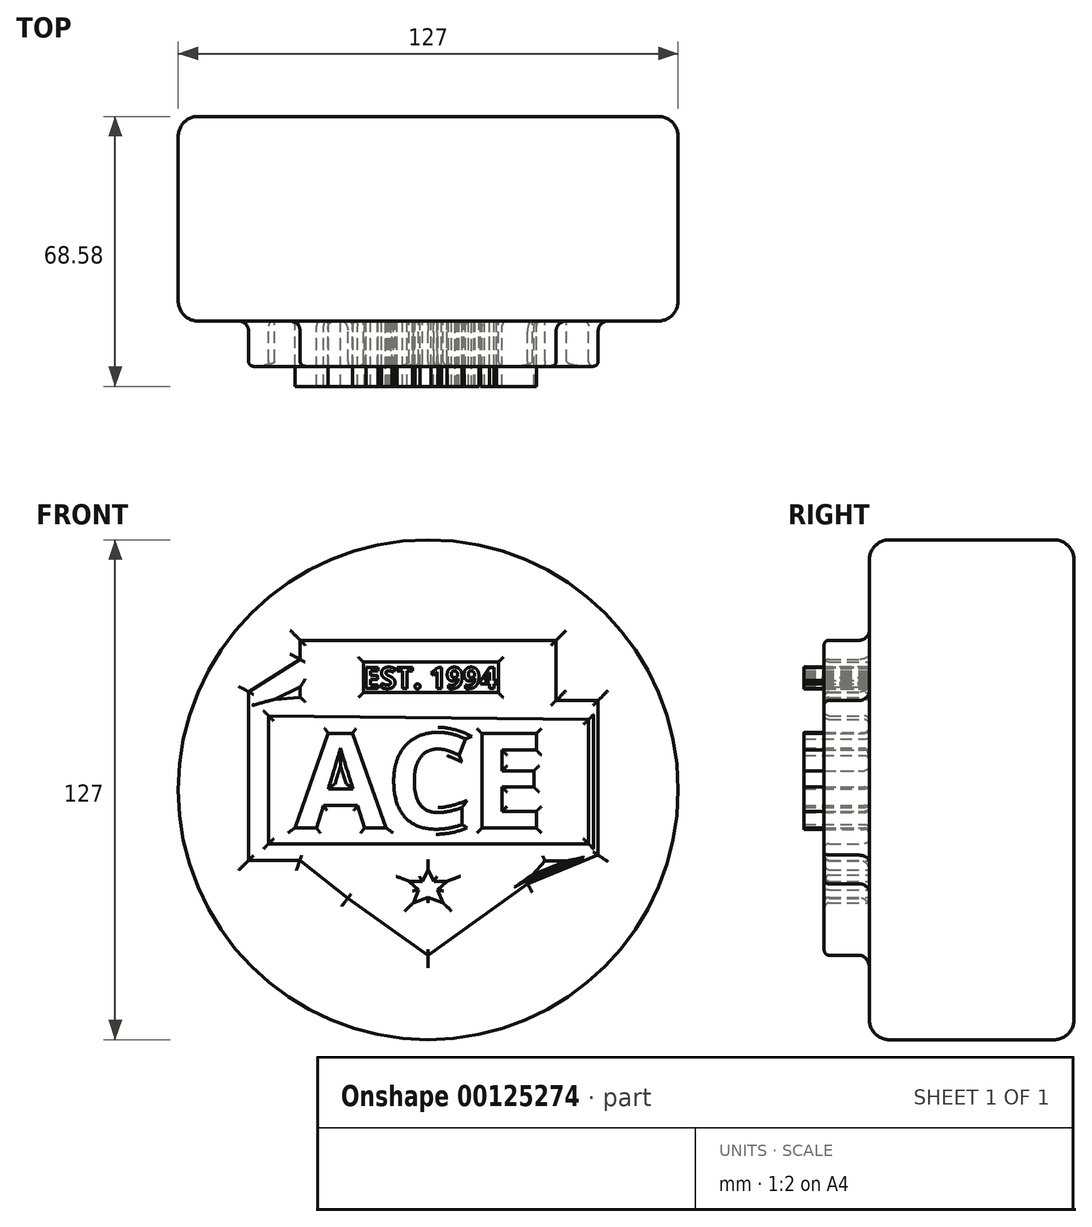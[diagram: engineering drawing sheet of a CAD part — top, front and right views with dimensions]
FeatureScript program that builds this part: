
annotation { "Feature Type Name" : "Feature", "Feature Type Description" : "" }
export const myFeature = defineFeature(function(context is Context, id is Id, definition is map)
    precondition{}
    {
        {
            var Q0;
            Q0=qCreatedBy(makeId("Front.planeOp"),FACE);
            var sketch = newSketch(context, id + "F0", { "sketchPlane" : qUnion([Q0])});
            skLineSegment(sketch, "E0", {"start": v(-32.51, 28.27) * mm, "end": v(-32.51, 37.97) * mm});
            skLineSegment(sketch, "E1", {"start": v(-32.51, 37.97) * mm, "end": v(32.51, 37.97) * mm});
            skLineSegment(sketch, "E2", {"start": v(32.51, 37.97) * mm, "end": v(32.51, 22.69) * mm});
            skLineSegment(sketch, "E3", {"start": v(32.51, 22.69) * mm, "end": v(43.19, 22.69) * mm});
            skLineSegment(sketch, "E4", {"start": v(43.19, 22.69) * mm, "end": v(43.19, -16.62) * mm});
            skLineSegment(sketch, "E5", {"start": v(43.19, -16.62) * mm, "end": v(25.23, -23.9) * mm});
            skLineSegment(sketch, "E6", {"start": v(25.23, -23.9) * mm, "end": v(0, -42.08) * mm});
            skLineSegment(sketch, "E7", {"start": v(0, -42.08) * mm, "end": v(-20.4, -27.54) * mm});
            skLineSegment(sketch, "E8", {"start": v(-20.4, -27.54) * mm, "end": v(-32.58, -17.93) * mm});
            skLineSegment(sketch, "E9", {"start": v(-32.58, -17.93) * mm, "end": v(-45.61, -17.93) * mm});
            skLineSegment(sketch, "E10", {"start": v(-45.61, -17.93) * mm, "end": v(-45.61, 21.23) * mm});
            skLineSegment(sketch, "E11", {"start": v(-45.61, 21.23) * mm, "end": v(-33.73, 21.23) * mm});
            skLineSegment(sketch, "E12", {"start": v(-32.51, 28.27) * mm, "end": v(-32.51, 21.23) * mm});
            skLineSegment(sketch, "E13", {"start": v(-45.61, 21.23) * mm, "end": v(-32.51, 28.27) * mm});
            skLineSegment(sketch, "E14", {"start": v(-45.61, 24.87) * mm, "end": v(-32.51, 33.12) * mm});
            skLineSegment(sketch, "E15", {"start": v(-32.51, 33.12) * mm, "end": v(-45.61, 24.87) * mm});
            skLineSegment(sketch, "E16", {"start": v(-45.61, 21.23) * mm, "end": v(-45.61, 24.87) * mm});
            skLineSegment(sketch, "E17", {"start": v(-40.55, 18.8) * mm, "end": v(-40.55, -13.7) * mm});
            skLineSegment(sketch, "E18", {"start": v(-40.55, -13.7) * mm, "end": v(40.73, -13.7) * mm});
            skLineSegment(sketch, "E19", {"start": v(40.73, -13.7) * mm, "end": v(40.73, 17.82) * mm});
            skLineSegment(sketch, "E20", {"start": v(40.73, 17.82) * mm, "end": v(-40.55, 18.8) * mm});
            skText(sketch, "E21", { "text": "ACE", "fontName": "OpenSans-Bold.ttf"});
            skText(sketch, "E22", { "text": "EST. 1994", "fontName": "OpenSans-Bold.ttf"});
            skLineSegment(sketch, "E23", {"start": v(26.46, -21.62) * mm, "end": v(35.2, -18.08) * mm});
            skLineSegment(sketch, "E24", {"start": v(35.2, -18.08) * mm, "end": v(29.69, -18.08) * mm});
            skLineSegment(sketch, "E25", {"start": v(29.69, -18.08) * mm, "end": v(26.46, -21.62) * mm});
            skLineSegment(sketch, "E26", {"start": v(0, -20.42) * mm, "end": v(-1.49, -23.24) * mm});
            skLineSegment(sketch, "E27", {"start": v(-1.49, -23.24) * mm, "end": v(-4.85, -23.24) * mm});
            skLineSegment(sketch, "E28", {"start": v(-4.85, -23.24) * mm, "end": v(-2.43, -25.39) * mm});
            skLineSegment(sketch, "E29", {"start": v(-2.43, -25.39) * mm, "end": v(-3.77, -28.75) * mm});
            skLineSegment(sketch, "E30", {"start": v(-3.77, -28.75) * mm, "end": v(0, -27.4) * mm});
            skLineSegment(sketch, "E31", {"start": v(0, -20.42) * mm, "end": v(0, -27.4) * mm});
            skLineSegment(sketch, "E32.MirrorCS", {"start": v(2.43, -25.39) * mm, "end": v(3.77, -28.75) * mm});
            skLineSegment(sketch, "E33.MirrorCS", {"start": v(3.77, -28.75) * mm, "end": v(0, -27.4) * mm});
            skLineSegment(sketch, "E34.MirrorCS", {"start": v(4.85, -23.24) * mm, "end": v(2.43, -25.39) * mm});
            skLineSegment(sketch, "E35.MirrorCS", {"start": v(1.49, -23.24) * mm, "end": v(4.85, -23.24) * mm});
            skLineSegment(sketch, "E36.MirrorCS", {"start": v(0, -20.42) * mm, "end": v(1.49, -23.24) * mm});
            skLineSegment(sketch, "E37", {"start": v(-32.51, 21.23) * mm, "end": v(-33.73, 21.23) * mm});
            skLineSegment(sketch, "E38", {"start": v(-38.98, 22.99) * mm, "end": v(-32.51, 26.1) * mm});
            skLineSegment(sketch, "E39", {"start": v(-32.51, 26.1) * mm, "end": v(-32.51, 23.5) * mm});
            skLineSegment(sketch, "E40", {"start": v(-32.51, 23.5) * mm, "end": v(-38.98, 22.99) * mm});
            skLineSegment(sketch, "E41.bottom", {"start": v(-16.45, 32.41) * mm, "end": v(17.83, 32.41) * mm});
            skLineSegment(sketch, "E41.top", {"start": v(-16.45, 24.65) * mm, "end": v(17.83, 24.65) * mm});
            skLineSegment(sketch, "E41.left", {"start": v(-16.45, 32.41) * mm, "end": v(-16.45, 24.65) * mm});
            skLineSegment(sketch, "E41.right", {"start": v(17.83, 32.41) * mm, "end": v(17.83, 24.65) * mm});
            const initialGuessF0  = {"E21": [-0.03384, -0.0097, 1, 0, 0.02415], "E22": [-0.01645, 0.02573, 1, 0, 0.0054]};
            skSetInitialGuess(sketch, initialGuessF0);
            skSolve(sketch);
        }
        {
            var Q0;
            Q0=makeQuery(id+"F0.imprint","IMPRINT",FACE,{"disambiguationData":[TD([[makeQuery(id+"F0.imprint","IMPRINT",EDGE,{"derivedFrom":sQuery(id+"F0.wireOp",EDGE,"E22.sketch_text.stroke-0")}),-1.0]])]});
            var Q1;
            Q1=makeQuery(id+"F0.imprint","IMPRINT",FACE,{"disambiguationData":[TD([[makeQuery(id+"F0.imprint","IMPRINT",EDGE,{"derivedFrom":sQuery(id+"F0.wireOp",EDGE,"E22.sketch_text.stroke-12")}),-1.0]])]});
            var Q2;
            Q2=makeQuery(id+"F0.imprint","IMPRINT",FACE,{"disambiguationData":[TD([[makeQuery(id+"F0.imprint","IMPRINT",EDGE,{"derivedFrom":sQuery(id+"F0.wireOp",EDGE,"E22.sketch_text.stroke-40")}),-1.0]])]});
            var Q3;
            Q3=makeQuery(id+"F0.imprint","IMPRINT",FACE,{"disambiguationData":[TD([[makeQuery(id+"F0.imprint","IMPRINT",EDGE,{"derivedFrom":sQuery(id+"F0.wireOp",EDGE,"E22.sketch_text.stroke-48")}),-1.0]])]});
            var Q4;
            Q4=makeQuery(id+"F0.imprint","IMPRINT",FACE,{"disambiguationData":[TD([[makeQuery(id+"F0.imprint","IMPRINT",EDGE,{"derivedFrom":sQuery(id+"F0.wireOp",EDGE,"E22.sketch_text.stroke-56")}),-1.0]])]});
            var Q5;
            Q5=makeQuery(id+"F0.imprint","IMPRINT",FACE,{"disambiguationData":[TD([[makeQuery(id+"F0.imprint","IMPRINT",EDGE,{"derivedFrom":sQuery(id+"F0.wireOp",EDGE,"E22.sketch_text.stroke-66")}),-1.0]])]});
            var Q6;
            Q6=makeQuery(id+"F0.imprint","IMPRINT",FACE,{"disambiguationData":[TD([[makeQuery(id+"F0.imprint","IMPRINT",EDGE,{"derivedFrom":sQuery(id+"F0.wireOp",EDGE,"E22.sketch_text.stroke-92")}),-1.0]])]});
            var Q7;
            Q7=makeQuery(id+"F0.imprint","IMPRINT",FACE,{"disambiguationData":[TD([[makeQuery(id+"F0.imprint","IMPRINT",EDGE,{"derivedFrom":sQuery(id+"F0.wireOp",EDGE,"E22.sketch_text.stroke-118")}),-1.0]])]});
            var Q8;
            {var subQ5=sQuery(id+"F0.wireOp",EDGE,"E1");Q8=makeQuery(id+"F0.imprint","IMPRINT",FACE,{"disambiguationData":[TD([[makeQuery(id+"F0.imprint","IMPRINT",EDGE,{"derivedFrom":subQ5}),-1.0]])]});}
            var Q9;
            Q9=makeQuery(id+"F0.imprint","IMPRINT",FACE,{"disambiguationData":[TD([[makeQuery(id+"F0.imprint","IMPRINT",EDGE,{"derivedFrom":sQuery(id+"F0.wireOp",EDGE,"E21.sketch_text.stroke-12")}),-1.0]])]});
            var Q10;
            Q10=makeQuery(id+"F0.imprint","IMPRINT",FACE,{"disambiguationData":[TD([[makeQuery(id+"F0.imprint","IMPRINT",EDGE,{"derivedFrom":sQuery(id+"F0.wireOp",EDGE,"E21.sketch_text.stroke-0")}),-1.0]])]});
            var Q11;
            Q11=makeQuery(id+"F0.imprint","IMPRINT",FACE,{"disambiguationData":[TD([[makeQuery(id+"F0.imprint","IMPRINT",EDGE,{"derivedFrom":sQuery(id+"F0.wireOp",EDGE,"E21.sketch_text.stroke-27")}),-1.0]])]});
            var Q12;
            {var subQ0=sQuery(id+"F0.wireOp",EDGE,"E13");Q12=makeQuery(id+"F0.imprint","IMPRINT",FACE,{"disambiguationData":[TD([[makeQuery(id+"F0.imprint","IMPRINT",EDGE,{"derivedFrom":subQ0}),1.0]])]});}
            var Q13;
            Q13=makeQuery(id+"F0.imprint","IMPRINT",FACE,{"disambiguationData":[TD([[makeQuery(id+"F0.imprint","IMPRINT",EDGE,{"derivedFrom":sQuery(id+"F0.wireOp",EDGE,"E11")}),1.0]])]});
            extrude(context, id + "F1", {"entities" : qUnion([Q0, Q1, Q2, Q3, Q4, Q5, Q6, Q7, Q8, Q9, Q10, Q11, Q12, Q13]), "depth" : 38.1 * mm, "hasSecondDirection" : true, "secondDirectionOppositeDirection" : false, "secondDirectionDepth" : 8.18 * mm});
        }
        {
            var Q0;
            Q0=qCreatedBy(makeId("Front.planeOp"),FACE);
            var sketch = newSketch(context, id + "F2", { "sketchPlane" : qUnion([Q0])});
            skCircle(sketch, "E42", {"center": v(0, 0) * mm, "radius": 63.5 * mm});
            skLineSegment(sketch, "E43", {"start": v(0, 63.5) * mm, "end": v(0, -63.5) * mm});
            skSolve(sketch);
        }
        {
            var Q0;
            Q0 = qSketchRegion(id + "F2", true);
            extrude(context, id + "F3", {"entities" : qUnion([Q0]), "operationType" : NewBodyOperationType.ADD, "depth" : 26.6 * mm, "hasSecondDirection" : true, "secondDirectionOppositeDirection" : true, "secondDirectionDepth" : 25.4 * mm});
        }
        {
            var Q0;
            Q0=makeQuery(id+"F1.opExtrude","CAP_FACE",FACE,{"disambiguationData":[OSD([sQuery(id+"F0.wireOp",EDGE,"E21.sketch_text.stroke-0"),sQuery(id+"F0.wireOp",EDGE,"E21.sketch_text.stroke-1"),sQuery(id+"F0.wireOp",EDGE,"E21.sketch_text.stroke-2"),sQuery(id+"F0.wireOp",EDGE,"E21.sketch_text.stroke-3"),sQuery(id+"F0.wireOp",EDGE,"E21.sketch_text.stroke-4"),sQuery(id+"F0.wireOp",EDGE,"E21.sketch_text.stroke-5"),sQuery(id+"F0.wireOp",EDGE,"E21.sketch_text.stroke-6"),sQuery(id+"F0.wireOp",EDGE,"E21.sketch_text.stroke-7"),sQuery(id+"F0.wireOp",EDGE,"E21.sketch_text.stroke-8"),sQuery(id+"F0.wireOp",EDGE,"E21.sketch_text.stroke-9"),sQuery(id+"F0.wireOp",EDGE,"E21.sketch_text.stroke-10"),sQuery(id+"F0.wireOp",EDGE,"E21.sketch_text.stroke-11")])],"isStart":false});
            var Q1;
            Q1=makeQuery(id+"F1.opExtrude","CAP_FACE",FACE,{"disambiguationData":[OSD([sQuery(id+"F0.wireOp",EDGE,"E21.sketch_text.stroke-12"),sQuery(id+"F0.wireOp",EDGE,"E21.sketch_text.stroke-13"),sQuery(id+"F0.wireOp",EDGE,"E21.sketch_text.stroke-14"),sQuery(id+"F0.wireOp",EDGE,"E21.sketch_text.stroke-15"),sQuery(id+"F0.wireOp",EDGE,"E21.sketch_text.stroke-16"),sQuery(id+"F0.wireOp",EDGE,"E21.sketch_text.stroke-17"),sQuery(id+"F0.wireOp",EDGE,"E21.sketch_text.stroke-18"),sQuery(id+"F0.wireOp",EDGE,"E21.sketch_text.stroke-19"),sQuery(id+"F0.wireOp",EDGE,"E21.sketch_text.stroke-20"),sQuery(id+"F0.wireOp",EDGE,"E21.sketch_text.stroke-21"),sQuery(id+"F0.wireOp",EDGE,"E21.sketch_text.stroke-22"),sQuery(id+"F0.wireOp",EDGE,"E21.sketch_text.stroke-23"),sQuery(id+"F0.wireOp",EDGE,"E21.sketch_text.stroke-24"),sQuery(id+"F0.wireOp",EDGE,"E21.sketch_text.stroke-25"),sQuery(id+"F0.wireOp",EDGE,"E21.sketch_text.stroke-26")])],"isStart":false});
            var Q2;
            Q2=makeQuery(id+"F1.opExtrude","CAP_FACE",FACE,{"disambiguationData":[OSD([sQuery(id+"F0.wireOp",EDGE,"E21.sketch_text.stroke-27"),sQuery(id+"F0.wireOp",EDGE,"E21.sketch_text.stroke-28"),sQuery(id+"F0.wireOp",EDGE,"E21.sketch_text.stroke-29"),sQuery(id+"F0.wireOp",EDGE,"E21.sketch_text.stroke-30"),sQuery(id+"F0.wireOp",EDGE,"E21.sketch_text.stroke-31"),sQuery(id+"F0.wireOp",EDGE,"E21.sketch_text.stroke-32"),sQuery(id+"F0.wireOp",EDGE,"E21.sketch_text.stroke-33"),sQuery(id+"F0.wireOp",EDGE,"E21.sketch_text.stroke-34"),sQuery(id+"F0.wireOp",EDGE,"E21.sketch_text.stroke-35"),sQuery(id+"F0.wireOp",EDGE,"E21.sketch_text.stroke-36"),sQuery(id+"F0.wireOp",EDGE,"E21.sketch_text.stroke-37"),sQuery(id+"F0.wireOp",EDGE,"E21.sketch_text.stroke-38")])],"isStart":false});
            var Q3;
            Q3=makeQuery(id+"F1.opExtrude","CAP_FACE",FACE,{"disambiguationData":[OSD([sQuery(id+"F0.wireOp",EDGE,"E22.sketch_text.stroke-0"),sQuery(id+"F0.wireOp",EDGE,"E22.sketch_text.stroke-1"),sQuery(id+"F0.wireOp",EDGE,"E22.sketch_text.stroke-2"),sQuery(id+"F0.wireOp",EDGE,"E22.sketch_text.stroke-3"),sQuery(id+"F0.wireOp",EDGE,"E22.sketch_text.stroke-4"),sQuery(id+"F0.wireOp",EDGE,"E22.sketch_text.stroke-5"),sQuery(id+"F0.wireOp",EDGE,"E22.sketch_text.stroke-6"),sQuery(id+"F0.wireOp",EDGE,"E22.sketch_text.stroke-7"),sQuery(id+"F0.wireOp",EDGE,"E22.sketch_text.stroke-8"),sQuery(id+"F0.wireOp",EDGE,"E22.sketch_text.stroke-9"),sQuery(id+"F0.wireOp",EDGE,"E22.sketch_text.stroke-10"),sQuery(id+"F0.wireOp",EDGE,"E22.sketch_text.stroke-11")])],"isStart":false});
            var Q4;
            Q4=makeQuery(id+"F1.opExtrude","CAP_FACE",FACE,{"disambiguationData":[OSD([sQuery(id+"F0.wireOp",EDGE,"E22.sketch_text.stroke-12"),sQuery(id+"F0.wireOp",EDGE,"E22.sketch_text.stroke-13"),sQuery(id+"F0.wireOp",EDGE,"E22.sketch_text.stroke-14"),sQuery(id+"F0.wireOp",EDGE,"E22.sketch_text.stroke-15"),sQuery(id+"F0.wireOp",EDGE,"E22.sketch_text.stroke-16"),sQuery(id+"F0.wireOp",EDGE,"E22.sketch_text.stroke-17"),sQuery(id+"F0.wireOp",EDGE,"E22.sketch_text.stroke-18"),sQuery(id+"F0.wireOp",EDGE,"E22.sketch_text.stroke-19"),sQuery(id+"F0.wireOp",EDGE,"E22.sketch_text.stroke-20"),sQuery(id+"F0.wireOp",EDGE,"E22.sketch_text.stroke-21"),sQuery(id+"F0.wireOp",EDGE,"E22.sketch_text.stroke-22"),sQuery(id+"F0.wireOp",EDGE,"E22.sketch_text.stroke-23"),sQuery(id+"F0.wireOp",EDGE,"E22.sketch_text.stroke-24"),sQuery(id+"F0.wireOp",EDGE,"E22.sketch_text.stroke-25"),sQuery(id+"F0.wireOp",EDGE,"E22.sketch_text.stroke-26"),sQuery(id+"F0.wireOp",EDGE,"E22.sketch_text.stroke-27"),sQuery(id+"F0.wireOp",EDGE,"E22.sketch_text.stroke-28"),sQuery(id+"F0.wireOp",EDGE,"E22.sketch_text.stroke-29"),sQuery(id+"F0.wireOp",EDGE,"E22.sketch_text.stroke-30"),sQuery(id+"F0.wireOp",EDGE,"E22.sketch_text.stroke-31"),sQuery(id+"F0.wireOp",EDGE,"E22.sketch_text.stroke-32"),sQuery(id+"F0.wireOp",EDGE,"E22.sketch_text.stroke-33"),sQuery(id+"F0.wireOp",EDGE,"E22.sketch_text.stroke-34"),sQuery(id+"F0.wireOp",EDGE,"E22.sketch_text.stroke-35"),sQuery(id+"F0.wireOp",EDGE,"E22.sketch_text.stroke-36"),sQuery(id+"F0.wireOp",EDGE,"E22.sketch_text.stroke-37"),sQuery(id+"F0.wireOp",EDGE,"E22.sketch_text.stroke-38"),sQuery(id+"F0.wireOp",EDGE,"E22.sketch_text.stroke-39")])],"isStart":false});
            var Q5;
            Q5=makeQuery(id+"F1.opExtrude","CAP_FACE",FACE,{"disambiguationData":[OSD([sQuery(id+"F0.wireOp",EDGE,"E22.sketch_text.stroke-40"),sQuery(id+"F0.wireOp",EDGE,"E22.sketch_text.stroke-41"),sQuery(id+"F0.wireOp",EDGE,"E22.sketch_text.stroke-42"),sQuery(id+"F0.wireOp",EDGE,"E22.sketch_text.stroke-43"),sQuery(id+"F0.wireOp",EDGE,"E22.sketch_text.stroke-44"),sQuery(id+"F0.wireOp",EDGE,"E22.sketch_text.stroke-45"),sQuery(id+"F0.wireOp",EDGE,"E22.sketch_text.stroke-46"),sQuery(id+"F0.wireOp",EDGE,"E22.sketch_text.stroke-47")])],"isStart":false});
            var Q6;
            Q6=makeQuery(id+"F1.opExtrude","CAP_FACE",FACE,{"disambiguationData":[OSD([sQuery(id+"F0.wireOp",EDGE,"E22.sketch_text.stroke-48"),sQuery(id+"F0.wireOp",EDGE,"E22.sketch_text.stroke-49"),sQuery(id+"F0.wireOp",EDGE,"E22.sketch_text.stroke-50"),sQuery(id+"F0.wireOp",EDGE,"E22.sketch_text.stroke-51"),sQuery(id+"F0.wireOp",EDGE,"E22.sketch_text.stroke-52"),sQuery(id+"F0.wireOp",EDGE,"E22.sketch_text.stroke-53"),sQuery(id+"F0.wireOp",EDGE,"E22.sketch_text.stroke-54"),sQuery(id+"F0.wireOp",EDGE,"E22.sketch_text.stroke-55")])],"isStart":false});
            var Q7;
            Q7=makeQuery(id+"F1.opExtrude","CAP_FACE",FACE,{"disambiguationData":[OSD([sQuery(id+"F0.wireOp",EDGE,"E22.sketch_text.stroke-56"),sQuery(id+"F0.wireOp",EDGE,"E22.sketch_text.stroke-57"),sQuery(id+"F0.wireOp",EDGE,"E22.sketch_text.stroke-58"),sQuery(id+"F0.wireOp",EDGE,"E22.sketch_text.stroke-59"),sQuery(id+"F0.wireOp",EDGE,"E22.sketch_text.stroke-60"),sQuery(id+"F0.wireOp",EDGE,"E22.sketch_text.stroke-61"),sQuery(id+"F0.wireOp",EDGE,"E22.sketch_text.stroke-62"),sQuery(id+"F0.wireOp",EDGE,"E22.sketch_text.stroke-63"),sQuery(id+"F0.wireOp",EDGE,"E22.sketch_text.stroke-64"),sQuery(id+"F0.wireOp",EDGE,"E22.sketch_text.stroke-65")])],"isStart":false});
            var Q8;
            Q8=makeQuery(id+"F1.opExtrude","CAP_FACE",FACE,{"disambiguationData":[OSD([sQuery(id+"F0.wireOp",EDGE,"E22.sketch_text.stroke-66"),sQuery(id+"F0.wireOp",EDGE,"E22.sketch_text.stroke-67"),sQuery(id+"F0.wireOp",EDGE,"E22.sketch_text.stroke-68"),sQuery(id+"F0.wireOp",EDGE,"E22.sketch_text.stroke-69"),sQuery(id+"F0.wireOp",EDGE,"E22.sketch_text.stroke-70"),sQuery(id+"F0.wireOp",EDGE,"E22.sketch_text.stroke-71"),sQuery(id+"F0.wireOp",EDGE,"E22.sketch_text.stroke-72"),sQuery(id+"F0.wireOp",EDGE,"E22.sketch_text.stroke-73"),sQuery(id+"F0.wireOp",EDGE,"E22.sketch_text.stroke-74"),sQuery(id+"F0.wireOp",EDGE,"E22.sketch_text.stroke-75"),sQuery(id+"F0.wireOp",EDGE,"E22.sketch_text.stroke-76"),sQuery(id+"F0.wireOp",EDGE,"E22.sketch_text.stroke-77"),sQuery(id+"F0.wireOp",EDGE,"E22.sketch_text.stroke-78"),sQuery(id+"F0.wireOp",EDGE,"E22.sketch_text.stroke-79"),sQuery(id+"F0.wireOp",EDGE,"E22.sketch_text.stroke-80"),sQuery(id+"F0.wireOp",EDGE,"E22.sketch_text.stroke-81"),sQuery(id+"F0.wireOp",EDGE,"E22.sketch_text.stroke-82"),sQuery(id+"F0.wireOp",EDGE,"E22.sketch_text.stroke-83"),sQuery(id+"F0.wireOp",EDGE,"E22.sketch_text.stroke-84"),sQuery(id+"F0.wireOp",EDGE,"E22.sketch_text.stroke-85"),sQuery(id+"F0.wireOp",EDGE,"E22.sketch_text.stroke-86"),sQuery(id+"F0.wireOp",EDGE,"E22.sketch_text.stroke-87"),sQuery(id+"F0.wireOp",EDGE,"E22.sketch_text.stroke-88"),sQuery(id+"F0.wireOp",EDGE,"E22.sketch_text.stroke-89"),sQuery(id+"F0.wireOp",EDGE,"E22.sketch_text.stroke-90"),sQuery(id+"F0.wireOp",EDGE,"E22.sketch_text.stroke-91")])],"isStart":false});
            var Q9;
            Q9=makeQuery(id+"F1.opExtrude","CAP_FACE",FACE,{"disambiguationData":[OSD([sQuery(id+"F0.wireOp",EDGE,"E22.sketch_text.stroke-92"),sQuery(id+"F0.wireOp",EDGE,"E22.sketch_text.stroke-93"),sQuery(id+"F0.wireOp",EDGE,"E22.sketch_text.stroke-94"),sQuery(id+"F0.wireOp",EDGE,"E22.sketch_text.stroke-95"),sQuery(id+"F0.wireOp",EDGE,"E22.sketch_text.stroke-96"),sQuery(id+"F0.wireOp",EDGE,"E22.sketch_text.stroke-97"),sQuery(id+"F0.wireOp",EDGE,"E22.sketch_text.stroke-98"),sQuery(id+"F0.wireOp",EDGE,"E22.sketch_text.stroke-99"),sQuery(id+"F0.wireOp",EDGE,"E22.sketch_text.stroke-100"),sQuery(id+"F0.wireOp",EDGE,"E22.sketch_text.stroke-101"),sQuery(id+"F0.wireOp",EDGE,"E22.sketch_text.stroke-102"),sQuery(id+"F0.wireOp",EDGE,"E22.sketch_text.stroke-103"),sQuery(id+"F0.wireOp",EDGE,"E22.sketch_text.stroke-104"),sQuery(id+"F0.wireOp",EDGE,"E22.sketch_text.stroke-105"),sQuery(id+"F0.wireOp",EDGE,"E22.sketch_text.stroke-106"),sQuery(id+"F0.wireOp",EDGE,"E22.sketch_text.stroke-107"),sQuery(id+"F0.wireOp",EDGE,"E22.sketch_text.stroke-108"),sQuery(id+"F0.wireOp",EDGE,"E22.sketch_text.stroke-109"),sQuery(id+"F0.wireOp",EDGE,"E22.sketch_text.stroke-110"),sQuery(id+"F0.wireOp",EDGE,"E22.sketch_text.stroke-111"),sQuery(id+"F0.wireOp",EDGE,"E22.sketch_text.stroke-112"),sQuery(id+"F0.wireOp",EDGE,"E22.sketch_text.stroke-113"),sQuery(id+"F0.wireOp",EDGE,"E22.sketch_text.stroke-114"),sQuery(id+"F0.wireOp",EDGE,"E22.sketch_text.stroke-115"),sQuery(id+"F0.wireOp",EDGE,"E22.sketch_text.stroke-116"),sQuery(id+"F0.wireOp",EDGE,"E22.sketch_text.stroke-117")])],"isStart":false});
            var Q10;
            Q10=makeQuery(id+"F1.opExtrude","CAP_FACE",FACE,{"disambiguationData":[OSD([sQuery(id+"F0.wireOp",EDGE,"E22.sketch_text.stroke-118"),sQuery(id+"F0.wireOp",EDGE,"E22.sketch_text.stroke-119"),sQuery(id+"F0.wireOp",EDGE,"E22.sketch_text.stroke-120"),sQuery(id+"F0.wireOp",EDGE,"E22.sketch_text.stroke-121"),sQuery(id+"F0.wireOp",EDGE,"E22.sketch_text.stroke-122"),sQuery(id+"F0.wireOp",EDGE,"E22.sketch_text.stroke-123"),sQuery(id+"F0.wireOp",EDGE,"E22.sketch_text.stroke-124"),sQuery(id+"F0.wireOp",EDGE,"E22.sketch_text.stroke-125"),sQuery(id+"F0.wireOp",EDGE,"E22.sketch_text.stroke-126"),sQuery(id+"F0.wireOp",EDGE,"E22.sketch_text.stroke-127"),sQuery(id+"F0.wireOp",EDGE,"E22.sketch_text.stroke-128"),sQuery(id+"F0.wireOp",EDGE,"E22.sketch_text.stroke-129"),sQuery(id+"F0.wireOp",EDGE,"E22.sketch_text.stroke-130"),sQuery(id+"F0.wireOp",EDGE,"E22.sketch_text.stroke-131"),sQuery(id+"F0.wireOp",EDGE,"E22.sketch_text.stroke-132"),sQuery(id+"F0.wireOp",EDGE,"E22.sketch_text.stroke-133"),sQuery(id+"F0.wireOp",EDGE,"E22.sketch_text.stroke-134"),sQuery(id+"F0.wireOp",EDGE,"E22.sketch_text.stroke-135")])],"isStart":false});
            extrude(context, id + "F4", {"entities" : qUnion([Q0, Q1, Q2, Q3, Q4, Q5, Q6, Q7, Q8, Q9, Q10]), "operationType" : NewBodyOperationType.ADD, "depth" : 5.08 * mm});
        }
        {
            var Q0;
            Q0=makeQuery(id+"F3.boolean.opBoolean","SPLIT",FACE,{"disambiguationData":[TD([makeQuery(id+"F1.opExtrude","SWEPT_FACE",FACE,{"disambiguationData":[OSD([sQuery(id+"F0.wireOp",EDGE,"E17")])]})])],"derivedFrom":makeQuery(id+"F3.opExtrude","CAP_FACE",FACE,{"disambiguationData":[OSD([sQuery(id+"F2.wireOp",EDGE,"E42")])],"isStart":false})});
            var Q1;
            Q1=makeQuery(id+"F3.boolean.opBoolean","SPLIT",FACE,{"disambiguationData":[TD([makeQuery(id+"F1.opExtrude","SWEPT_FACE",FACE,{"disambiguationData":[OSD([sQuery(id+"F0.wireOp",EDGE,"E21.sketch_text.stroke-8")])]})])],"derivedFrom":makeQuery(id+"F3.opExtrude","CAP_FACE",FACE,{"disambiguationData":[OSD([sQuery(id+"F2.wireOp",EDGE,"E42")])],"isStart":false})});
            var Q2;
            Q2=makeQuery(id+"F1.opExtrude","CAP_EDGE",EDGE,{"disambiguationData":[OSD([sQuery(id+"F0.wireOp",EDGE,"E41.top")])],"isStart":false});
            var Q3;
            Q3=makeQuery(id+"F1.opExtrude","CAP_EDGE",EDGE,{"disambiguationData":[OSD([sQuery(id+"F0.wireOp",EDGE,"E41.left")])],"isStart":false});
            var Q4;
            Q4=makeQuery(id+"F1.opExtrude","CAP_EDGE",EDGE,{"disambiguationData":[OSD([sQuery(id+"F0.wireOp",EDGE,"E41.right")])],"isStart":false});
            var Q5;
            Q5=makeQuery(id+"F1.opExtrude","CAP_EDGE",EDGE,{"disambiguationData":[OSD([sQuery(id+"F0.wireOp",EDGE,"E41.bottom")])],"isStart":false});
            var Q6;
            Q6=makeQuery(id+"F1.opExtrude","CAP_FACE",FACE,{"disambiguationData":[OSD([sQuery(id+"F0.wireOp",EDGE,"E0"),sQuery(id+"F0.wireOp",EDGE,"E1"),sQuery(id+"F0.wireOp",EDGE,"E2"),sQuery(id+"F0.wireOp",EDGE,"E3"),sQuery(id+"F0.wireOp",EDGE,"E4"),sQuery(id+"F0.wireOp",EDGE,"E5"),sQuery(id+"F0.wireOp",EDGE,"E6"),sQuery(id+"F0.wireOp",EDGE,"E7"),sQuery(id+"F0.wireOp",EDGE,"E8"),sQuery(id+"F0.wireOp",EDGE,"E9"),sQuery(id+"F0.wireOp",EDGE,"E10"),sQuery(id+"F0.wireOp",EDGE,"E15"),sQuery(id+"F0.wireOp",EDGE,"E16"),sQuery(id+"F0.wireOp",EDGE,"E17"),sQuery(id+"F0.wireOp",EDGE,"E18"),sQuery(id+"F0.wireOp",EDGE,"E19"),sQuery(id+"F0.wireOp",EDGE,"E20"),sQuery(id+"F0.wireOp",EDGE,"E23"),sQuery(id+"F0.wireOp",EDGE,"E24"),sQuery(id+"F0.wireOp",EDGE,"E25"),sQuery(id+"F0.wireOp",EDGE,"E26"),sQuery(id+"F0.wireOp",EDGE,"E27"),sQuery(id+"F0.wireOp",EDGE,"E28"),sQuery(id+"F0.wireOp",EDGE,"E29"),sQuery(id+"F0.wireOp",EDGE,"E30"),sQuery(id+"F0.wireOp",EDGE,"E32.MirrorCS"),sQuery(id+"F0.wireOp",EDGE,"E33.MirrorCS"),sQuery(id+"F0.wireOp",EDGE,"E34.MirrorCS"),sQuery(id+"F0.wireOp",EDGE,"E35.MirrorCS"),sQuery(id+"F0.wireOp",EDGE,"E36.MirrorCS"),sQuery(id+"F0.wireOp",EDGE,"E38"),sQuery(id+"F0.wireOp",EDGE,"E39"),sQuery(id+"F0.wireOp",EDGE,"E40"),sQuery(id+"F0.wireOp",EDGE,"E41.bottom"),sQuery(id+"F0.wireOp",EDGE,"E41.top"),sQuery(id+"F0.wireOp",EDGE,"E41.left"),sQuery(id+"F0.wireOp",EDGE,"E41.right")])],"isStart":false});
            fillet(context, id + "F5", {"entities" : qUnion([Q0, Q1, Q2, Q3, Q4, Q5, Q6]), "radius" : 1.27 * mm, "tangentPropagation" : true, "allowEdgeOverflow" : false});
        }
        {
            var Q0;
            Q0=makeQuery(id+"F3.opExtrude","CAP_EDGE",EDGE,{"disambiguationData":[OSD([sQuery(id+"F2.wireOp",EDGE,"E42")])],"isStart":false});
            var Q1;
            Q1=makeQuery(id+"F3.opExtrude","CAP_EDGE",EDGE,{"disambiguationData":[OSD([sQuery(id+"F2.wireOp",EDGE,"E42")])],"isStart":true});
            fillet(context, id + "F6", {"entities" : qUnion([Q0, Q1]), "radius" : 5.08 * mm, "tangentPropagation" : true, "allowEdgeOverflow" : false});
        }
        {
            var Q0;
            {var subQ0=sQuery(id+"F2.wireOp",EDGE,"E42");Q0=makeQuery(id+"F3.boolean.opBoolean","SPLIT",FACE,{"disambiguationData":[TD([makeQuery(id+"F1.opExtrude","SWEPT_FACE",FACE,{"disambiguationData":[OSD([sQuery(id+"F0.wireOp",EDGE,"E0")])]})])],"derivedFrom":makeQuery(id+"F3.opExtrude","CAP_FACE",FACE,{"disambiguationData":[OSD([subQ0])],"isStart":false})});}
            fillet(context, id + "F7", {"entities" : qUnion([Q0]), "radius" : 2.54 * mm, "tangentPropagation" : true, "allowEdgeOverflow" : false});
        }
    });
